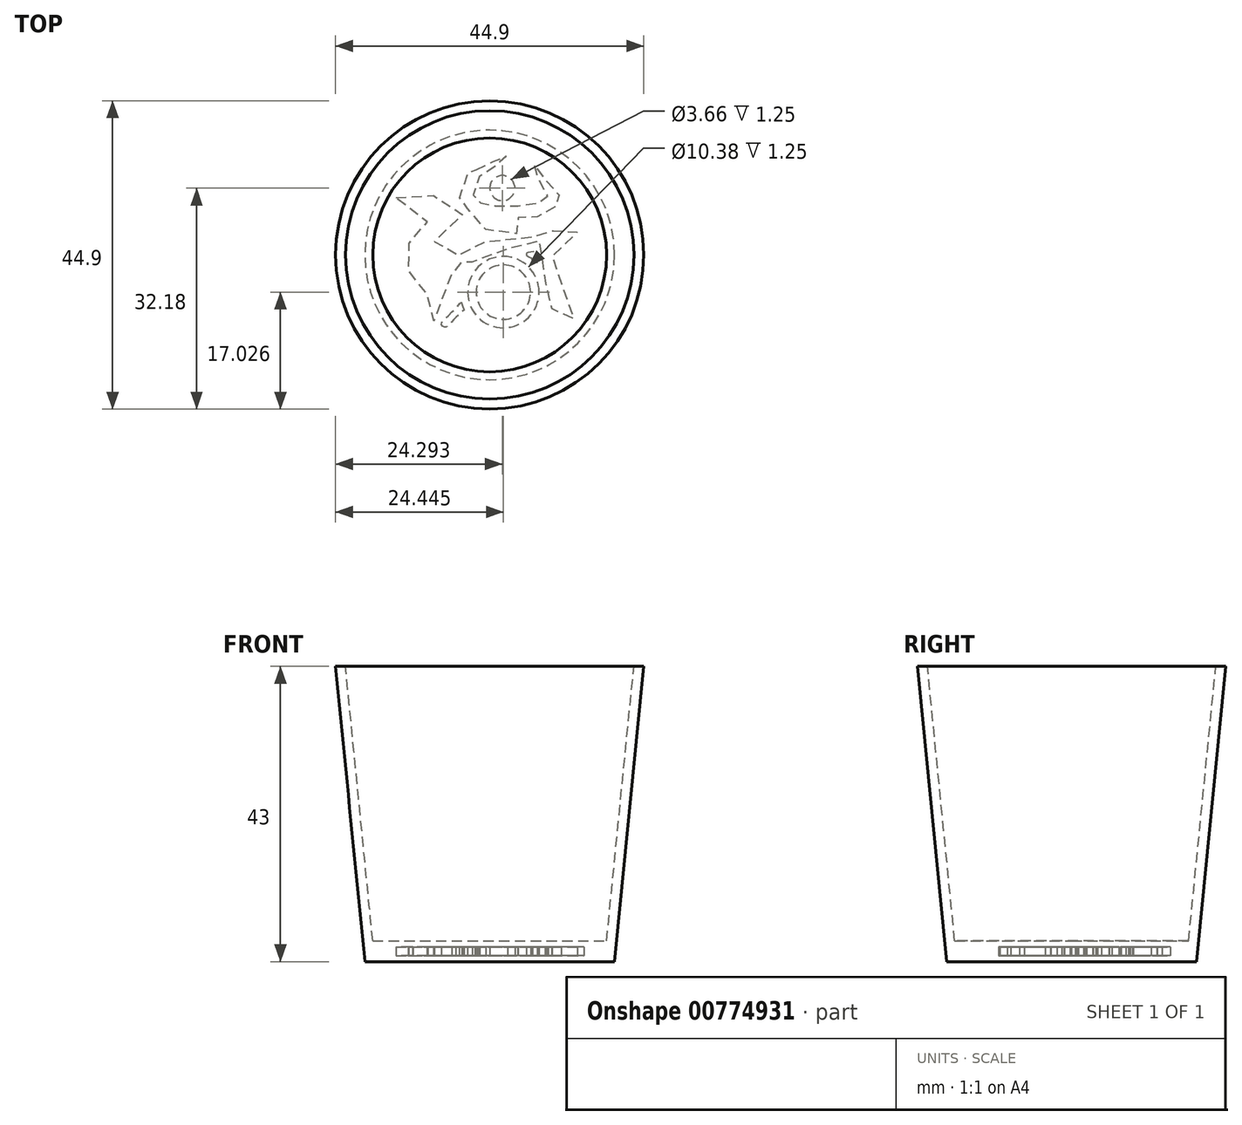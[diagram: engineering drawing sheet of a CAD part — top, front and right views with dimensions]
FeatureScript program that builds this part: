
annotation { "Feature Type Name" : "Feature", "Feature Type Description" : "" }
export const myFeature = defineFeature(function(context is Context, id is Id, definition is map)
    precondition{}
    {
        {
            var Q0;
            Q0=qCreatedBy(makeId("Front.planeOp"),FACE);
            var sketch = newSketch(context, id + "F0", { "sketchPlane" : qUnion([Q0])});
            skLineSegment(sketch, "E0", {"start": v(22.45, 43) * mm, "end": v(21, 43) * mm});
            skLineSegment(sketch, "E1", {"start": v(21, 43) * mm, "end": v(17.03, 3) * mm});
            skLineSegment(sketch, "E2", {"start": v(17.03, 3) * mm, "end": v(0, 3) * mm});
            skLineSegment(sketch, "E3", {"start": v(15.16, 0) * mm, "end": v(0, 0) * mm});
            skLineSegment(sketch, "E4", {"start": v(0, 0) * mm, "end": v(0, 3) * mm});
            skLineSegment(sketch, "E5", {"start": v(15.16, 0) * mm, "end": v(18.18, 0) * mm});
            skLineSegment(sketch, "E6", {"start": v(22.45, 43) * mm, "end": v(18.18, 0) * mm});
            skPoint(sketch, "E7.orphan", {"position": v(21.26, 0) * mm});
            skSolve(sketch);
        }
        {
            var Q0;
            Q0=qSketchRegion(id+"F0",true);
            var Q1;
            Q1=sQuery(id+"F0.wireOp",EDGE,"E4");
            revolve(context, id + "F1", {"surfaceOperationType" : NewSurfaceOperationType.NEW, "entities" : qUnion([Q0]), "axis" : qUnion([Q1]), "revolveType" : RevolveType.FULL});
        }
        {
            var Q0;
            Q0=qCreatedBy(makeId("Top.planeOp"),FACE);
            cPlane(context, id + "F2", {"entities" : qUnion([Q0]), "cplaneType" : CPlaneType.OFFSET, "offset" : 1.5 * mm, "width" : 150 * mm, "height" : 150 * mm});
        }
        {
            var Q0;
            Q0=qCreatedBy(id+"F2.planeOp",FACE);
            var sketch = newSketch(context, id + "F3", { "sketchPlane" : qUnion([Q0])});
            skFitSpline(sketch, "E8", {"points": [v(-13.66, 8.35) * mm, v(-12.15, 8.52) * mm, v(-10.61, 8.5) * mm, v(-9.42, 8.3) * mm, v(-9.1, 8.32) * mm, v(-9.04, 8.6) * mm, v(-8.61, 8.95) * mm, v(-8.2, 8.66) * mm, v(-8.13, 8.12) * mm, v(-8.1, 8.01) * mm, v(-7.15, 7.7) * mm, v(-6.07, 7.27) * mm, v(-5.15, 6.75) * mm, v(-3.96, 6.08) * mm, v(-3.83, 5.9) * mm, v(-4.16, 5.9) * mm, v(-6.38, 6.46) * mm, v(-7.96, 6.86) * mm, v(-8.05, 6.86) * mm, v(-8.07, 6.46) * mm, v(-8.07, 1.94) * mm, v(-8.02, 1.9) * mm, v(-5.5, 1.92) * mm, v(-5.06, 1.74) * mm, v(-5, 1.25) * mm, v(-5.33, 0.89) * mm, v(-5.49, 0.86) * mm, v(-5.48, 0) * mm, v(-5.33, -0.04) * mm, v(-1.8, -0.06) * mm, v(-1.68, -0.01) * mm, v(-1.68, 0.32) * mm, v(-1.7, 0.85) * mm, v(-1.78, 0.9) * mm, v(-2.1, 1.13) * mm, v(-2.07, 1.67) * mm, v(-1.53, 1.88) * mm, v(0.6, 1.9) * mm, v(3.43, 1.9) * mm, v(4.27, 1.87) * mm, v(4.51, 1.76) * mm, v(4.74, 1.8) * mm, v(5.28, 2.11) * mm, v(6.26, 2.68) * mm, v(7.72, 3.2) * mm, v(8.17, 3.34) * mm, v(8.12, 3.6) * mm, v(8.21, 4.06) * mm, v(8.57, 4.34) * mm, v(8.93, 4.2) * mm, v(9.08, 3.8) * mm, v(9.1, 3.5) * mm, v(9.25, 3.54) * mm, v(9.9, 3.7) * mm, v(11.26, 3.75) * mm, v(12.15, 3.77) * mm, v(12.97, 3.72) * mm, v(13.66, 3.7) * mm, v(13.66, 3.5) * mm, v(12.88, 3.32) * mm, v(11.78, 3.05) * mm, v(10.77, 2.8) * mm, v(10.15, 2.69) * mm, v(9.35, 2.48) * mm, v(9.08, 2.4) * mm, v(9.07, 2.13) * mm, v(9.09, -1.13) * mm, v(9.02, -5.98) * mm, v(9.12, -6.2) * mm, v(10.61, -7.63) * mm, v(12.01, -9.1) * mm, v(12.74, -9.9) * mm, v(12.74, -10.27) * mm, v(12.43, -10.43) * mm, v(12.17, -10.46) * mm, v(11.7, -10.05) * mm, v(9.34, -7.73) * mm, v(9.06, -7.6) * mm, v(9.12, -8.2) * mm, v(8.9, -8.78) * mm, v(8.32, -8.78) * mm, v(8.1, -8.05) * mm, v(8.13, -6.92) * mm, v(8.33, -5.31) * mm, v(8.22, -4.15) * mm, v(8.11, -3.63) * mm, v(8.1, -1.35) * mm, v(8.11, 0.64) * mm, v(8.13, 2.1) * mm, v(8.11, 2.2) * mm, v(7.38, 2.03) * mm, v(5.56, 1.55) * mm, v(4.7, 1.33) * mm, v(4.61, 1.19) * mm, v(4.48, 1) * mm, v(4.23, 0.92) * mm, v(4.14, 0.85) * mm, v(4.16, 0.64) * mm, v(4.15, 0.55) * mm, v(3.55, 0.78) * mm, v(1.83, 0.94) * mm, v(0.7, 0.8) * mm, v(-0.14, 0.59) * mm, v(-1.2, 0.08) * mm, v(-1.38, -0.08) * mm, v(-1.8, -0.42) * mm, v(-2.18, -0.65) * mm, v(-3.6, -2.3) * mm, v(-3.88, -3.14) * mm, v(-4.04, -3.83) * mm, v(-4.06, -2.77) * mm, v(-4.05, -1.84) * mm, v(-4.05, -1.14) * mm, v(-4.05, -1.1) * mm, v(-4.43, -1.1) * mm, v(-5.42, -1.09) * mm, v(-5.47, -1.18) * mm, v(-5.51, -1.68) * mm, v(-5.48, -2.1) * mm, v(-5.35, -2.12) * mm, v(-5.02, -2.33) * mm, v(-4.97, -2.74) * mm, v(-5.18, -2.98) * mm, v(-5.26, -3.03) * mm, v(-5.46, -3.04) * mm, v(-7.94, -3.01) * mm, v(-8.12, -3.07) * mm, v(-8.1, -3.52) * mm, v(-8.15, -7.66) * mm, v(-8.15, -9.17) * mm, v(-8.12, -10.17) * mm, v(-8.19, -10.33) * mm, v(-8.46, -10.52) * mm, v(-8.77, -10.5) * mm, v(-8.96, -10.3) * mm, v(-9.1, -10.03) * mm, v(-9.04, -8.29) * mm, v(-9.1, -5.76) * mm, v(-9.08, -3.88) * mm, v(-9.04, -3.2) * mm, v(-9.08, -3.04) * mm, v(-9.42, -3.07) * mm, v(-11.4, -3.03) * mm, v(-11.7, -2.9) * mm, v(-11.78, -2.55) * mm, v(-11.75, -2.29) * mm, v(-11.46, -2.15) * mm, v(-11.22, -2.02) * mm, v(-11.19, 0) * mm, v(-11.19, 0.63) * mm, v(-11.24, 0.89) * mm, v(-11.44, 0.93) * mm, v(-11.77, 1.16) * mm, v(-11.86, 1.5) * mm, v(-11.75, 1.69) * mm, v(-11.58, 1.83) * mm, v(-11.3, 1.9) * mm, v(-10.97, 1.93) * mm, v(-10.43, 1.92) * mm, v(-9.76, 1.91) * mm, v(-9.3, 1.9) * mm, v(-9.22, 1.9) * mm, v(-9.13, 1.9) * mm, v(-9.1, 2) * mm, v(-9.1, 5.64) * mm, v(-9.11, 6.43) * mm, v(-9.12, 7.02) * mm, v(-9.18, 7.15) * mm, v(-9.99, 7.33) * mm, v(-12.26, 7.85) * mm, v(-13.66, 8.35) * mm]});
            skFitSpline(sketch, "E9", {"points": [v(5.35, -0.07) * mm, v(5.6, -0.19) * mm, v(6.01, -0.5) * mm, v(6.41, -0.86) * mm, v(6.67, -1.13) * mm, v(6.92, -1.44) * mm, v(6.92, -1.35) * mm, v(6.91, -0.4) * mm, v(6.92, 0.34) * mm, v(6.9, 0.64) * mm, v(6.8, 0.6) * mm, v(6.23, 0.46) * mm, v(5.44, 0.29) * mm, v(5.36, 0.26) * mm, v(5.35, -0.07) * mm]});
            skFitSpline(sketch, "E10", {"points": [v(-4.1, -6.9) * mm, v(-4.03, -7.23) * mm, v(-3.87, -7.7) * mm, v(-3.72, -8) * mm, v(-3.98, -8.27) * mm, v(-4.83, -9.06) * mm, v(-5.58, -9.8) * mm, v(-6.24, -10.46) * mm, v(-6.6, -10.54) * mm, v(-6.92, -10.33) * mm, v(-7.02, -10.08) * mm, v(-6.92, -9.74) * mm, v(-6.6, -9.42) * mm, v(-5.37, -8.18) * mm, v(-4.59, -7.4) * mm, v(-4.1, -6.9) * mm]});
            skCircle(sketch, "E11", {"center": v(2, -5.42) * mm, "radius": 3.96 * mm});
            skCircle(sketch, "E12", {"center": v(2, -5.42) * mm, "radius": 5.2 * mm});
            skCircle(sketch, "E13", {"center": v(1.84, 9.73) * mm, "radius": 1.83 * mm});
            skFitSpline(sketch, "E14", {"points": [v(-1.95, 12.44) * mm, v(-1.18, 12.85) * mm, v(-0.4, 13.18) * mm, v(0.41, 13.53) * mm, v(0.86, 13.72) * mm, v(1.48, 13.96) * mm, v(1.87, 14.15) * mm, v(2.26, 14.3) * mm, v(2.41, 14.36) * mm, v(2.62, 14.22) * mm, v(2.57, 13.98) * mm, v(2.11, 13.66) * mm, v(1.13, 13.12) * mm, v(-1.1, 11.9) * mm, v(-1.4, 11.74) * mm, v(-1.47, 11.64) * mm, v(-1.46, 11.54) * mm, v(-1.57, 11.2) * mm, v(-2.08, 9.65) * mm, v(-2.27, 9.2) * mm, v(-2.4, 8.75) * mm, v(-2.52, 8.43) * mm, v(-2.52, 8.33) * mm, v(-2.27, 8.15) * mm, v(-1.8, 7.9) * mm, v(-1.38, 7.63) * mm, v(-1, 7.42) * mm, v(-0.7, 7.26) * mm, v(-0.57, 7.2) * mm, v(-0.35, 7.2) * mm, v(0.86, 7.15) * mm, v(1.6, 7.15) * mm, v(3.09, 7.15) * mm, v(4.84, 7.16) * mm, v(6.33, 7.18) * mm, v(6.44, 7.18) * mm, v(6.6, 7.27) * mm, v(7.52, 7.82) * mm, v(7.8, 7.97) * mm, v(8.11, 8.17) * mm, v(8.48, 8.38) * mm, v(8.54, 8.47) * mm, v(8.43, 8.61) * mm, v(7.96, 9.55) * mm, v(7.56, 10.3) * mm, v(6.72, 11.87) * mm, v(6.34, 12.6) * mm, v(6.28, 12.81) * mm, v(6.27, 13) * mm, v(6.35, 13.09) * mm, v(6.44, 13.13) * mm, v(6.56, 13.12) * mm, v(6.62, 13.07) * mm, v(6.73, 12.95) * mm, v(6.97, 12.59) * mm, v(8, 11.07) * mm, v(9.4, 8.9) * mm, v(9.44, 8.86) * mm, v(9.67, 8.88) * mm, v(9.97, 8.8) * mm, v(10.31, 8.48) * mm, v(10.44, 7.9) * mm, v(10.2, 7.45) * mm, v(9.81, 7.17) * mm, v(9.33, 6.9) * mm, v(7.35, 5.74) * mm, v(7.21, 5.65) * mm, v(7.01, 5.55) * mm, v(6.62, 5.51) * mm, v(5, 5.46) * mm, v(4.34, 5.46) * mm, v(4.17, 5.45) * mm, v(4.07, 5.35) * mm, v(4.08, 5.11) * mm, v(4.09, 3.35) * mm, v(4.06, 3.13) * mm, v(3.84, 3.1) * mm, v(-0.45, 3.1) * mm, v(-0.56, 3.1) * mm, v(-0.56, 5.1) * mm, v(-0.56, 5.18) * mm, v(-0.68, 5.25) * mm, v(-4, 7.24) * mm, v(-4.19, 7.38) * mm, v(-4.3, 7.59) * mm, v(-4.4, 7.92) * mm, v(-4.4, 8.22) * mm, v(-4.34, 8.4) * mm, v(-3.84, 9.88) * mm, v(-3.14, 11.9) * mm, v(-3.02, 12.14) * mm, v(-2.88, 12.29) * mm, v(-2.73, 12.4) * mm, v(-2.46, 12.48) * mm, v(-2.23, 12.47) * mm, v(-2.1, 12.45) * mm, v(-1.95, 12.44) * mm]});
            skSolve(sketch);
        }
        {
            var Q0;
            Q0=qSketchRegion(id+"F3",true);
            extrude(context, id + "F4", {"entities" : qUnion([Q0]), "operationType" : NewBodyOperationType.REMOVE, "endBound" : BoundingType.SYMMETRIC, "depth" : 1.25 * mm, "offsetDistance" : 25 * mm});
        }
        {
            var Q0;
            Q0=qCreatedBy(makeId("Front.planeOp"),FACE);
            cPlane(context, id + "F5", {"entities" : qUnion([Q0]), "cplaneType" : CPlaneType.OFFSET, "offset" : 22 * mm, "width" : 150 * mm, "height" : 150 * mm});
        }
        {
            var Q0;
            Q0=qCreatedBy(id+"F5.planeOp",FACE);
            var sketch = newSketch(context, id + "F6", { "sketchPlane" : qUnion([Q0])});
            skText(sketch, "E15", { "text": "LEONIDAS\n     2017", "fontName": "Tinos-BoldItalic.ttf"});
            const initialGuessF6  = {"E15": [-0.01412, 0.02555, 1, 0, 0.004]};
            skSetInitialGuess(sketch, initialGuessF6);
            skSolve(sketch);
        }
        {
            var Q0;
            Q0=qSketchRegion(id+"F6",true);
            extrude(context, id + "F7", {"entities" : qUnion([Q0]), "operationType" : NewBodyOperationType.REMOVE, "depth" : 25 * mm, "offsetDistance" : 25 * mm});
        }
    });
